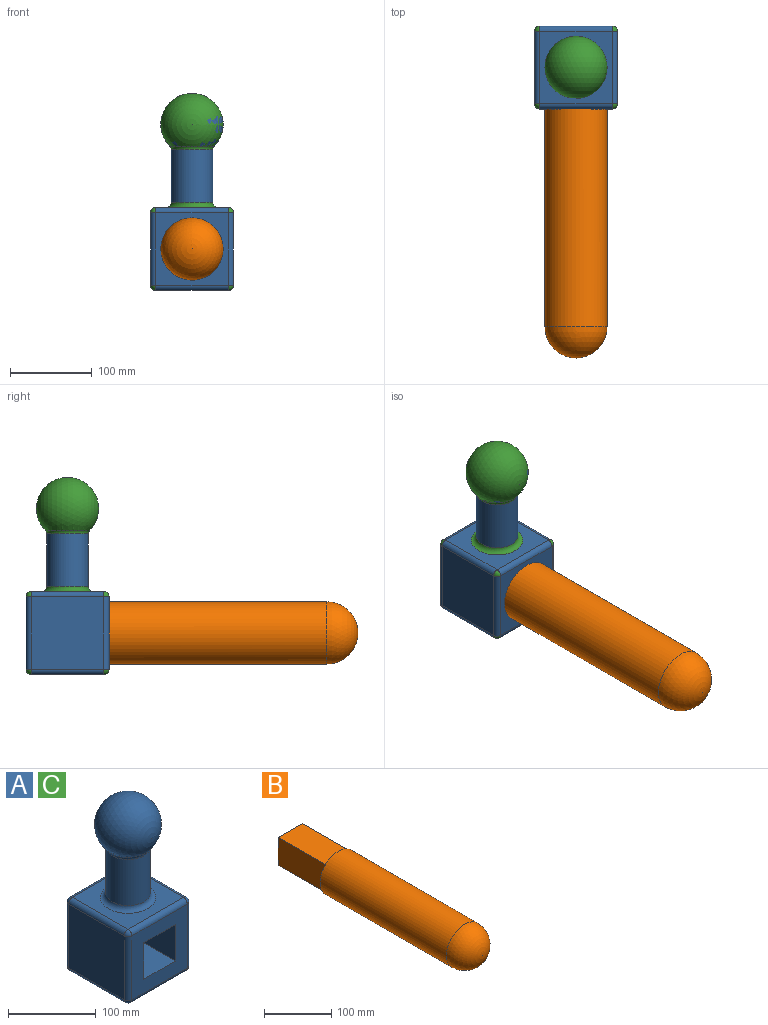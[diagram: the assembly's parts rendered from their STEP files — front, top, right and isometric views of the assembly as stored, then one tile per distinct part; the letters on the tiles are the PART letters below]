
ASSEMBLY  parts=3 mates=1
PART A: 34 faces, bbox 101.6x101.6x241.3 mm
  f0: plane 88.9x88.9mm, normal (0,-1,0), area 5322.6mm2, adj f8,f9,f10,f11,f22,f27,f30,f33
  f1: plane 88.9x88.9mm, normal (1,0,0), area 7903.2mm2, adj f19,f28,f29,f33
  f2: plane 88.9x88.9mm, normal (0,1,0), area 5322.6mm2, adj f8,f9,f10,f11,f14,f18,f19,f20
  f3: plane 88.9x88.9mm, normal (-1,0,0), area 7903.2mm2, adj f14,f17,f21,f22
  f4: plane 88.9x88.9mm, normal (0,0,1), area 4736.3mm2, adj f13,f17,f18,f27,f28
  f5: plane 88.9x88.9mm, normal (0,0,-1), area 7903.2mm2, adj f20,f21,f29,f30
  f6: cylinder r=25.4mm len=64.14mm, axis (0,0,-1), area 10236.5mm2, adj f12,f13
  f7: sphere r=38.1mm, area 15504.5mm2, adj f12
  f8: plane 101.6x50.8mm, normal (-1,0,0), area 5161.3mm2, adj f0,f2,f9,f11
  f9: plane 101.6x50.8mm, normal (0,0,-1), area 5161.3mm2, adj f0,f2,f8,f10
  f10: plane 101.6x50.8mm, normal (1,0,0), area 5161.3mm2, adj f0,f2,f9,f11
  f11: plane 101.6x50.8mm, normal (0,0,1), area 5161.3mm2, adj f0,f2,f8,f10
  f12: torus R=31.75mm, axis (0,0,1), area 804.7mm2, adj f6,f7
  f13: torus R=31.75mm, axis (0,0,1), area 1736.5mm2, adj f4,f6
  f14: cylinder r=6.35mm len=88.9mm, axis (0,0,-1), area 886.7mm2, adj f2,f3,f15,f16
  f15: sphere r=6.35mm, area 63.3mm2, adj f14,f17,f18
  f16: sphere r=6.35mm, area 63.3mm2, adj f14,f20,f21
  f17: cylinder r=6.35mm len=88.9mm, axis (0,1,0), area 886.7mm2, adj f3,f4,f15,f23
  f18: cylinder r=6.35mm len=88.9mm, axis (1,0,0), area 886.7mm2, adj f2,f4,f15,f24
  f19: cylinder r=6.35mm len=88.9mm, axis (0,0,1), area 886.7mm2, adj f1,f2,f24,f25
  f20: cylinder r=6.35mm len=88.9mm, axis (-1,0,0), area 886.7mm2, adj f2,f5,f16,f25
  f21: cylinder r=6.35mm len=88.9mm, axis (0,-1,0), area 886.7mm2, adj f3,f5,f16,f26
  f22: cylinder r=6.35mm len=88.9mm, axis (0,0,1), area 886.7mm2, adj f0,f3,f23,f26
  f23: sphere r=6.35mm, area 63.3mm2, adj f17,f22,f27
  f24: sphere r=6.35mm, area 63.3mm2, adj f18,f19,f28
  f25: sphere r=6.35mm, area 63.3mm2, adj f19,f20,f29
  f26: sphere r=6.35mm, area 63.3mm2, adj f21,f22,f30
  f27: cylinder r=6.35mm len=88.9mm, axis (-1,0,0), area 886.7mm2, adj f0,f4,f23,f31
  f28: cylinder r=6.35mm len=88.9mm, axis (0,-1,0), area 886.7mm2, adj f1,f4,f24,f31
  f29: cylinder r=6.35mm len=88.9mm, axis (0,1,0), area 886.7mm2, adj f1,f5,f25,f32
  f30: cylinder r=6.35mm len=88.9mm, axis (1,0,0), area 886.7mm2, adj f0,f5,f26,f32
  f31: sphere r=6.35mm, area 63.3mm2, adj f27,f28,f33
  f32: sphere r=6.35mm, area 63.3mm2, adj f29,f30,f33
  f33: cylinder r=6.35mm len=88.9mm, axis (0,0,-1), area 886.7mm2, adj f0,f1,f31,f32
PART B: 8 faces, bbox 76.2x406.4x76.2 mm
  f0: plane 101.6x50.8mm, normal (1,0,0), area 5161.3mm2, adj f1,f3,f4,f5
  f1: plane 101.6x50.8mm, normal (0,0,1), area 5161.3mm2, adj f0,f2,f4,f5
  f2: plane 101.6x50.8mm, normal (-1,0,0), area 5161.3mm2, adj f1,f3,f4,f5
  f3: plane 101.6x50.8mm, normal (0,0,-1), area 5161.3mm2, adj f0,f2,f4,f5
  f4: plane 50.8x50.8mm, normal (0,1,0), area 2580.6mm2, adj f0,f1,f2,f3
  f5: plane 76.2x76.2mm, normal (0,1,0), area 1979.7mm2, adj f0,f1,f2,f3,f6
  f6: cylinder r=38.1mm len=266.7mm, axis (0,1,0), area 63845.1mm2, adj f5,f7
  f7: sphere r=38.1mm, area 9120.7mm2, adj f6
PART C: same geometry as A
PLACE A t=(-29.53,19.63,-71.49)mm
PLACE B t=(-29.53,70.43,-20.69)mm
PLACE C t=(-29.53,19.63,-71.49)mm fixed
MATE fastened B.f6 <-> C.f2  axis (0,1,0) through (-29.53,70.43,-20.69)mm
